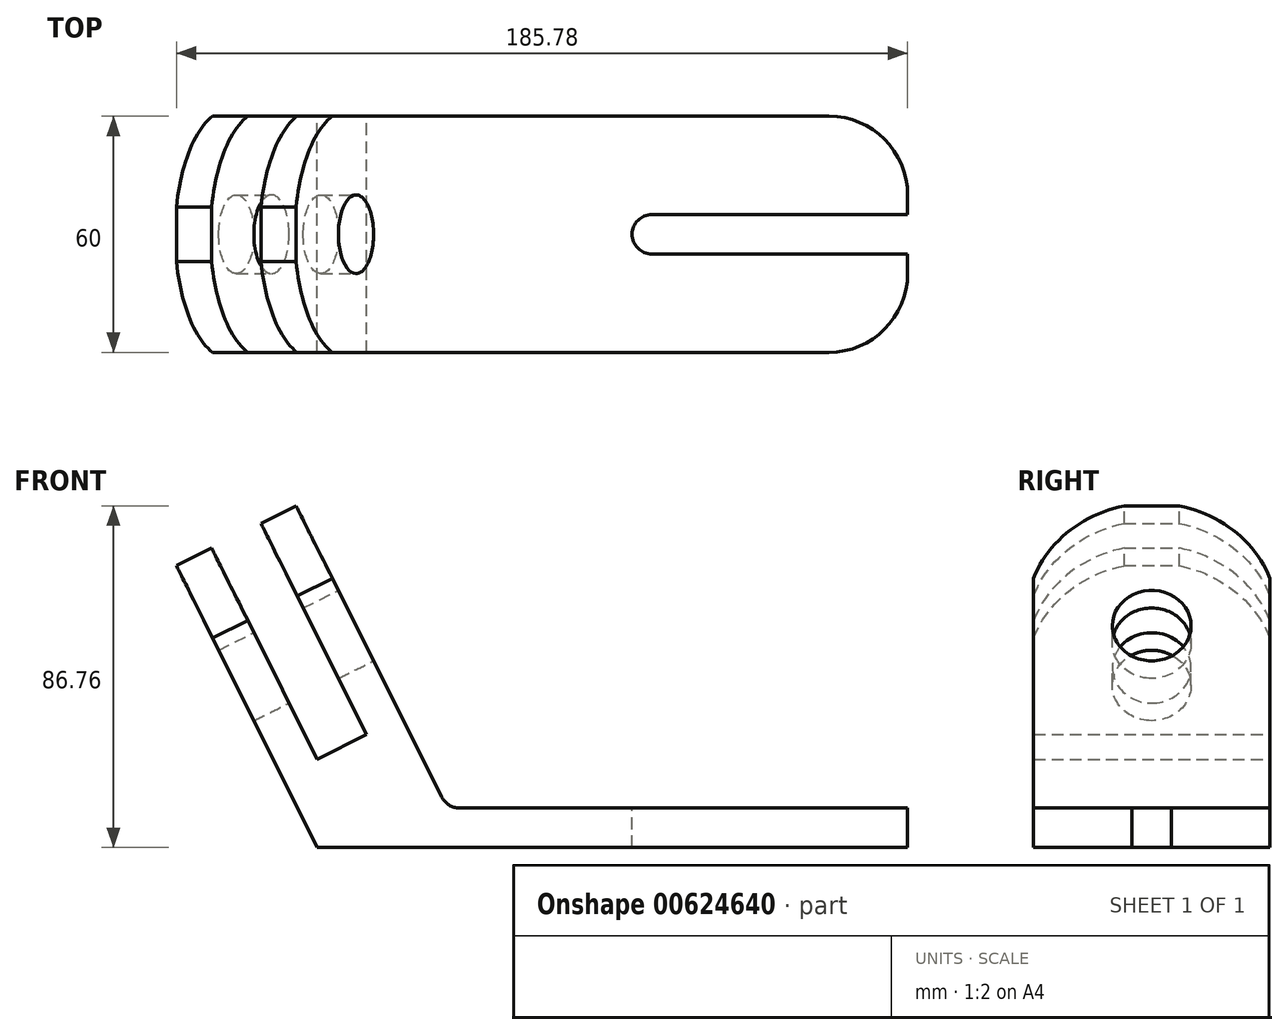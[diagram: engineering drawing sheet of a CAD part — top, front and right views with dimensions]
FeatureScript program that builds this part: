
annotation { "Feature Type Name" : "Feature", "Feature Type Description" : "" }
export const myFeature = defineFeature(function(context is Context, id is Id, definition is map)
    precondition{}
    {
        {
            var Q0;
            Q0=qCreatedBy(makeId("Front.planeOp"),FACE);
            var sketch = newSketch(context, id + "F0", { "sketchPlane" : qUnion([Q0])});
            skLineSegment(sketch, "E0", {"start": v(94.5, -11.12) * mm, "end": v(94.5, -21.12) * mm});
            skLineSegment(sketch, "E1", {"start": v(94.5, -21.12) * mm, "end": v(-55.5, -21.12) * mm});
            skLineSegment(sketch, "E2", {"start": v(-55.5, -21.12) * mm, "end": v(-91.27, 50.44) * mm});
            skLineSegment(sketch, "E3", {"start": v(-91.27, 50.44) * mm, "end": v(-82.33, 54.9) * mm});
            skLineSegment(sketch, "E4", {"start": v(-82.33, 54.9) * mm, "end": v(-55.5, 1.24) * mm});
            skLineSegment(sketch, "E5", {"start": v(-55.5, 1.24) * mm, "end": v(-42.97, 7.5) * mm});
            skLineSegment(sketch, "E6", {"start": v(-42.97, 7.5) * mm, "end": v(-69.8, 61.17) * mm});
            skLineSegment(sketch, "E7", {"start": v(-69.8, 61.17) * mm, "end": v(-60.86, 65.64) * mm});
            skLineSegment(sketch, "E8", {"start": v(-60.86, 65.64) * mm, "end": v(-23.86, -8.35) * mm});
            skLineSegment(sketch, "E9", {"start": v(-19.4, -11.12) * mm, "end": v(94.5, -11.12) * mm});
            skPoint(sketch, "E10.visualSharp", {"position": v(-22.48, -11.12) * mm});
            skArc(sketch, "E10.filletArc", {"start": v(-23.86, -8.35) * mm, "mid": v(-22.02, -10.37) * mm, "end": v(-19.4, -11.12) * mm});
            skSolve(sketch);
        }
        {
            var Q0;
            Q0 = qSketchRegion(id + "F0", true);
            extrude(context, id + "F1", {"entities" : qUnion([Q0]), "depth" : 60 * mm, "offsetDistance" : 25 * mm});
        }
        {
            var Q0;
            Q0=makeQuery(id+"F1.opExtrude","SWEPT_FACE",FACE,{"disambiguationData":[OSD([sQuery(id+"F0.wireOp",EDGE,"E9")])]});
            var sketch = newSketch(context, id + "F2", { "sketchPlane" : qUnion([Q0])});
            skArc(sketch, "E11", {"start": v(29.5, -25) * mm, "mid": v(24.5, -30) * mm, "end": v(29.5, -35) * mm});
            skPoint(sketch, "E11.centerSnap0", {"position": v(94.5, -30) * mm});
            skLineSegment(sketch, "E12", {"start": v(29.5, -25) * mm, "end": v(94.5, -25) * mm});
            skLineSegment(sketch, "E13", {"start": v(29.5, -35) * mm, "end": v(94.5, -35) * mm});
            skLineSegment(sketch, "E14", {"start": v(94.5, -35) * mm, "end": v(94.5, -25) * mm});
            skSolve(sketch);
        }
        {
            var Q0;
            Q0 = qSketchRegion(id + "F2", true);
            extrude(context, id + "F3", {"entities" : qUnion([Q0]), "operationType" : NewBodyOperationType.REMOVE, "oppositeDirection" : true, "depth" : 25 * mm, "offsetDistance" : 25 * mm});
        }
        {
            var Q0;
            Q0=makeQuery(id+"F1.opExtrude","SWEPT_FACE",FACE,{"disambiguationData":[OSD([sQuery(id+"F0.wireOp",EDGE,"E8")])]});
            var sketch = newSketch(context, id + "F4", { "sketchPlane" : qUnion([Q0])});
            skCircle(sketch, "E15", {"center": v(-30, 51.9) * mm, "radius": 10 * mm});
            skPoint(sketch, "E15.centerSnap0", {"position": v(-30, 85.93) * mm});
            skSolve(sketch);
        }
        {
            var Q0;
            Q0 = qSketchRegion(id + "F4", true);
            extrude(context, id + "F5", {"entities" : qUnion([Q0]), "operationType" : NewBodyOperationType.REMOVE, "oppositeDirection" : true, "depth" : 50.8 * mm, "offsetDistance" : 25 * mm});
        }
        {
            var Q0;
            Q0=makeQuery(id+"F1.opExtrude","SWEPT_FACE",FACE,{"disambiguationData":[OSD([sQuery(id+"F0.wireOp",EDGE,"E8")])]});
            var sketch = newSketch(context, id + "F6", { "sketchPlane" : qUnion([Q0])});
            skArc(sketch, "E16", {"start": v(0, 44.57) * mm, "mid": v(-30, 86.7) * mm, "end": v(-60, 44.57) * mm});
            skSolve(sketch);
        }
        {
            var Q0;
            Q0 = qSketchRegion(id + "F6", true);
            var Q1;
            {var subQ0=sQuery(id+"F6.wireOp",EDGE,"E16");var subQ1=sQuery(id+"F0.wireOp",EDGE,"E8");var subQ2=makeQuery(id+"F1.opExtrude","CAP_EDGE",EDGE,{"disambiguationData":[OSD([subQ1])],"isStart":true});var subQ3=makeQuery(id+"F6.imprint","INTERSECT",VERTEX,{"disambiguationData":[OD(1.0)],"derivedFrom":[subQ2,subQ0]});Q1=makeQuery(id+"F6.imprint","IMPRINT",FACE,{"disambiguationData":[TD([[makeQuery(id+"F6.imprint","IMPRINT",EDGE,{"disambiguationData":[TD([[subQ3,-1.0]])],"derivedFrom":subQ0}),-1.0]])]});}
            var Q2;
            {var subQ0=sQuery(id+"F6.wireOp",EDGE,"E16");var subQ1=sQuery(id+"F0.wireOp",EDGE,"E8");var subQ4=makeQuery(id+"F1.opExtrude","CAP_EDGE",EDGE,{"disambiguationData":[OSD([subQ1])],"isStart":false});var subQ5=makeQuery(id+"F6.imprint","INTERSECT",VERTEX,{"disambiguationData":[OD(1.0)],"derivedFrom":[subQ4,subQ0]});Q2=makeQuery(id+"F6.imprint","IMPRINT",FACE,{"disambiguationData":[TD([[makeQuery(id+"F6.imprint","IMPRINT",EDGE,{"disambiguationData":[TD([[subQ5,1.0]])],"derivedFrom":subQ0}),-1.0]])]});}
            extrude(context, id + "F7", {"entities" : qUnion([Q0, Q1, Q2]), "operationType" : NewBodyOperationType.REMOVE, "oppositeDirection" : true, "depth" : 42.5 * mm, "offsetDistance" : 25 * mm});
        }
        {
            var Q0;
            Q0=makeQuery(id+"F1.opExtrude","CAP_EDGE",EDGE,{"disambiguationData":[OSD([sQuery(id+"F0.wireOp",EDGE,"E0")])],"isStart":true});
            var Q1;
            Q1=makeQuery(id+"F1.opExtrude","CAP_EDGE",EDGE,{"disambiguationData":[OSD([sQuery(id+"F0.wireOp",EDGE,"E0")])],"isStart":false});
            fillet(context, id + "F8", {"entities" : qUnion([Q0, Q1]), "radius" : 20 * mm, "tangentPropagation" : true, "allowEdgeOverflow" : false});
        }
    });
